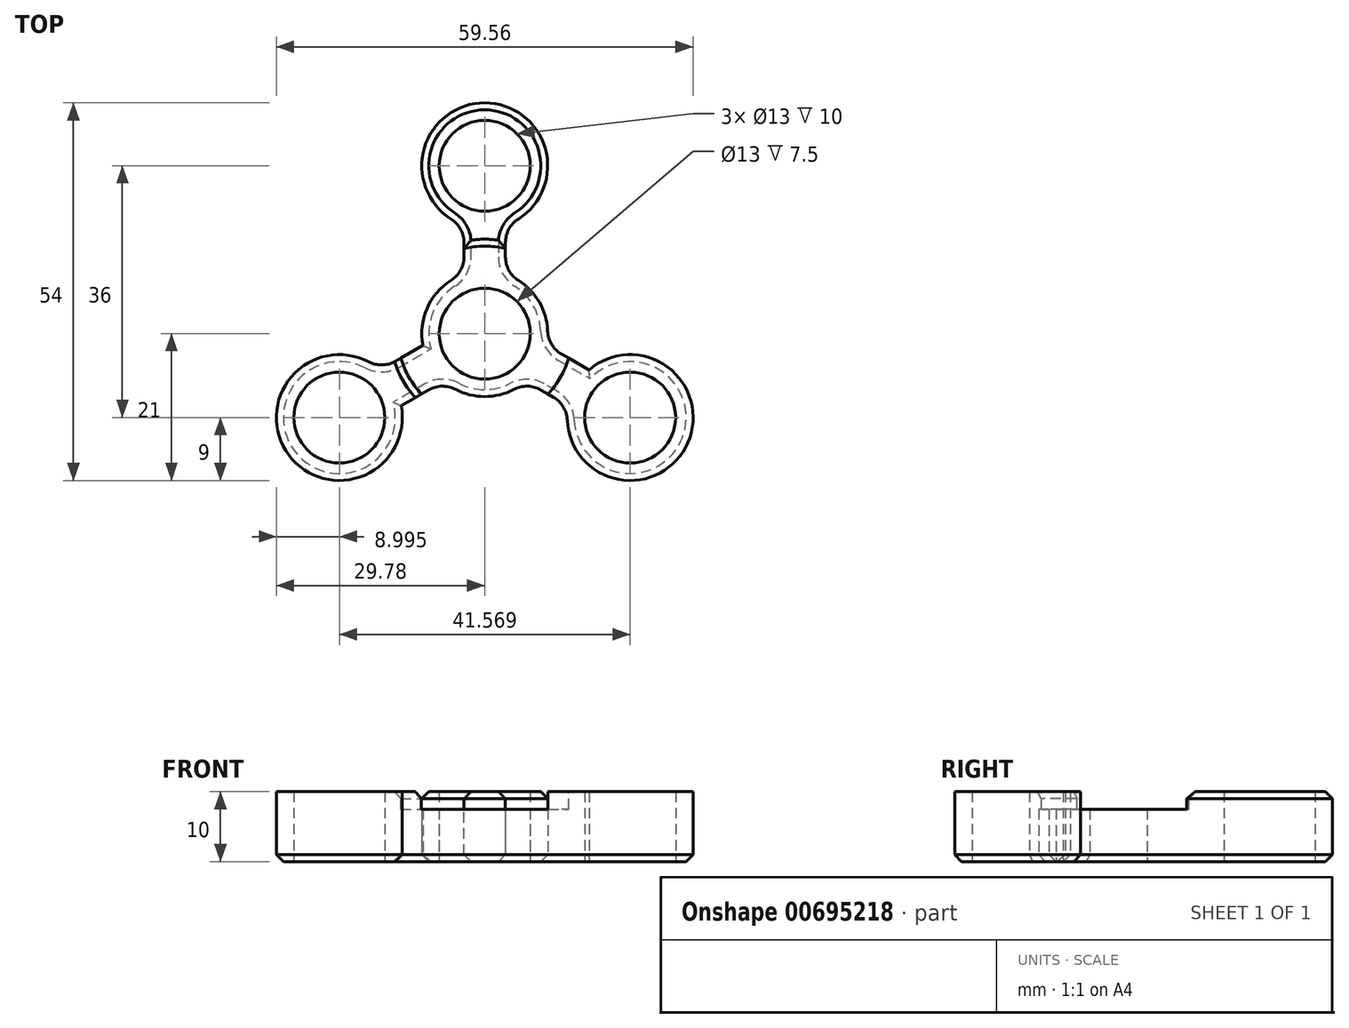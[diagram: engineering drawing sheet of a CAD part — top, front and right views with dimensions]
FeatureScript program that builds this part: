
annotation { "Feature Type Name" : "Feature", "Feature Type Description" : "" }
export const myFeature = defineFeature(function(context is Context, id is Id, definition is map)
    precondition{}
    {
        {
            var Q0;
            Q0=qCreatedBy(makeId("Top.planeOp"),FACE);
            var sketch = newSketch(context, id + "F0", { "sketchPlane" : qUnion([Q0])});
            skLineSegment(sketch, "E0", {"start": v(0, 0) * mm, "end": v(0, 24) * mm, "construction": true});
            skCircle(sketch, "E1", {"center": v(0, 24) * mm, "radius": 6.5 * mm});
            skPoint(sketch, "E2.center", {"position": v(0, 0) * mm});
            skCircle(sketch, "E3", {"center": v(0, 0) * mm, "radius": 6.5 * mm});
            skArc(sketch, "E4", {"start": v(2.96, 15.5) * mm, "mid": v(0, 33) * mm, "end": v(-2.96, 15.5) * mm});
            skCircle(sketch, "E5", {"center": v(0, 0) * mm, "radius": 9 * mm});
            skLineSegment(sketch, "E6", {"start": v(-2.96, 15.5) * mm, "end": v(-2.96, 8.5) * mm});
            skLineSegment(sketch, "E7.MirrorCS", {"start": v(2.96, 15.5) * mm, "end": v(2.96, 8.5) * mm});
            skArc(sketch, "E8.1.0", {"start": v(-14.9, -5.19) * mm, "mid": v(-28.58, -16.5) * mm, "end": v(-11.94, -10.31) * mm});
            skCircle(sketch, "E8.1.1", {"center": v(-20.78, -12) * mm, "radius": 6.5 * mm});
            skLineSegment(sketch, "E8.1.2", {"start": v(-11.94, -10.31) * mm, "end": v(-5.88, -6.81) * mm});
            skLineSegment(sketch, "E8.1.3", {"start": v(-14.9, -5.19) * mm, "end": v(-8.84, -1.69) * mm});
            skArc(sketch, "E8.2.0", {"start": v(11.94, -10.31) * mm, "mid": v(28.58, -16.5) * mm, "end": v(14.9, -5.19) * mm});
            skCircle(sketch, "E8.2.1", {"center": v(20.78, -12) * mm, "radius": 6.5 * mm});
            skLineSegment(sketch, "E8.2.2", {"start": v(14.9, -5.19) * mm, "end": v(8.84, -1.69) * mm});
            skLineSegment(sketch, "E8.2.3", {"start": v(11.94, -10.31) * mm, "end": v(5.88, -6.81) * mm});
            skSolve(sketch);
        }
        {
            var Q0;
            Q0=qSketchRegion(id+"F0",true);
            extrude(context, id + "F1", {"entities" : qUnion([Q0]), "endBound" : BoundingType.SYMMETRIC, "depth" : 10 * mm, "offsetDistance" : 25 * mm});
        }
        {
            var Q0;
            Q0=makeQuery(id+"F1.opExtrude","CAP_FACE",FACE,{"disambiguationData":[OSD([sQuery(id+"F0.wireOp",EDGE,"E1"),sQuery(id+"F0.wireOp",EDGE,"E3"),sQuery(id+"F0.wireOp",EDGE,"E4"),sQuery(id+"F0.wireOp",EDGE,"SNb2FpTf-bqCU-mBP4-37Ot-8CH4sN8bmC5e"),sQuery(id+"F0.wireOp",EDGE,"d9168214-b0ef-4c21-9807-18c6f3a28a83.1.0"),sQuery(id+"F0.wireOp",EDGE,"d9168214-b0ef-4c21-9807-18c6f3a28a83.1.1"),sQuery(id+"F0.wireOp",EDGE,"d9168214-b0ef-4c21-9807-18c6f3a28a83.2.0"),sQuery(id+"F0.wireOp",EDGE,"d9168214-b0ef-4c21-9807-18c6f3a28a83.2.1"),sQuery(id+"F0.wireOp",EDGE,"3bd34c21-cdaa-4902-b1d2-4efe5426a100.trimOffspring"),sQuery(id+"F0.wireOp",EDGE,"9c9765f9-2684-4891-bd0d-f60ce666e364.trimOffspring")])],"isStart":false});
            var sketch = newSketch(context, id + "F2", { "sketchPlane" : qUnion([Q0])});
            skCircle(sketch, "E9", {"center": v(0, 0) * mm, "radius": 12.5 * mm});
            skSolve(sketch);
        }
        {
            var Q0;
            Q0=qSketchRegion(id+"F2",true);
            extrude(context, id + "F3", {"entities" : qUnion([Q0]), "operationType" : NewBodyOperationType.REMOVE, "oppositeDirection" : true, "depth" : 2.5 * mm, "offsetDistance" : 25 * mm});
        }
        {
            var Q0;
            Q0=makeQuery(id+"F1.opExtrude","SWEPT_EDGE",EDGE,{"disambiguationData":[OSD([sQuery(id+"F0.wireOp",EDGE,"E4"),sQuery(id+"F0.wireOp",EDGE,"SNb2FpTf-bqCU-mBP4-37Ot-8CH4sN8bmC5e")])]});
            var Q1;
            Q1=makeQuery(id+"F1.opExtrude","SWEPT_EDGE",EDGE,{"disambiguationData":[OSD([sQuery(id+"F0.wireOp",EDGE,"E4"),sQuery(id+"F0.wireOp",EDGE,"9c9765f9-2684-4891-bd0d-f60ce666e364.trimOffspring")])]});
            var Q2;
            Q2=makeQuery(id+"F1.opExtrude","SWEPT_EDGE",EDGE,{"disambiguationData":[OSD([sQuery(id+"F0.wireOp",EDGE,"SNb2FpTf-bqCU-mBP4-37Ot-8CH4sN8bmC5e"),sQuery(id+"F0.wireOp",EDGE,"d9168214-b0ef-4c21-9807-18c6f3a28a83.1.0")])]});
            var Q3;
            Q3=makeQuery(id+"F1.opExtrude","SWEPT_EDGE",EDGE,{"disambiguationData":[OSD([sQuery(id+"F0.wireOp",EDGE,"d9168214-b0ef-4c21-9807-18c6f3a28a83.2.0"),sQuery(id+"F0.wireOp",EDGE,"9c9765f9-2684-4891-bd0d-f60ce666e364.trimOffspring")])]});
            var Q4;
            Q4=makeQuery(id+"F1.opExtrude","SWEPT_EDGE",EDGE,{"disambiguationData":[OSD([sQuery(id+"F0.wireOp",EDGE,"d9168214-b0ef-4c21-9807-18c6f3a28a83.2.0"),sQuery(id+"F0.wireOp",EDGE,"3bd34c21-cdaa-4902-b1d2-4efe5426a100.trimOffspring")])]});
            var Q5;
            Q5=makeQuery(id+"F1.opExtrude","SWEPT_EDGE",EDGE,{"disambiguationData":[OSD([sQuery(id+"F0.wireOp",EDGE,"d9168214-b0ef-4c21-9807-18c6f3a28a83.1.0"),sQuery(id+"F0.wireOp",EDGE,"3bd34c21-cdaa-4902-b1d2-4efe5426a100.trimOffspring")])]});
            var Q6;
            Q6=makeQuery(id+"F1.opExtrude","SWEPT_EDGE",EDGE,{"disambiguationData":[OSD([sQuery(id+"F0.wireOp",EDGE,"E5"),sQuery(id+"F0.wireOp",EDGE,"E6")])]});
            var Q7;
            Q7=makeQuery(id+"F1.opExtrude","SWEPT_EDGE",EDGE,{"disambiguationData":[OSD([sQuery(id+"F0.wireOp",EDGE,"E8.1.0"),sQuery(id+"F0.wireOp",EDGE,"E8.1.3")])]});
            var Q8;
            Q8=makeQuery(id+"F1.opExtrude","SWEPT_EDGE",EDGE,{"disambiguationData":[OSD([sQuery(id+"F0.wireOp",EDGE,"E8.2.0"),sQuery(id+"F0.wireOp",EDGE,"E8.2.3")])]});
            var Q9;
            Q9=makeQuery(id+"F1.opExtrude","SWEPT_EDGE",EDGE,{"disambiguationData":[OSD([sQuery(id+"F0.wireOp",EDGE,"E5"),sQuery(id+"F0.wireOp",EDGE,"E8.1.2")])]});
            var Q10;
            Q10=makeQuery(id+"F1.opExtrude","SWEPT_EDGE",EDGE,{"disambiguationData":[OSD([sQuery(id+"F0.wireOp",EDGE,"E5"),sQuery(id+"F0.wireOp",EDGE,"E8.2.3")])]});
            var Q11;
            Q11=makeQuery(id+"F1.opExtrude","SWEPT_EDGE",EDGE,{"disambiguationData":[OSD([sQuery(id+"F0.wireOp",EDGE,"E5"),sQuery(id+"F0.wireOp",EDGE,"E8.2.2")])]});
            var Q12;
            Q12=makeQuery(id+"F1.opExtrude","SWEPT_EDGE",EDGE,{"disambiguationData":[OSD([sQuery(id+"F0.wireOp",EDGE,"E5"),sQuery(id+"F0.wireOp",EDGE,"E7.MirrorCS")])]});
            fillet(context, id + "F4", {"entities" : qUnion([Q0, Q1, Q2, Q3, Q4, Q5, Q6, Q7, Q8, Q9, Q10, Q11, Q12]), "radius" : 4 * mm, "tangentPropagation" : true, "allowEdgeOverflow" : false});
        }
        {
            var Q0;
            Q0=makeQuery(id+"F1.opExtrude","CAP_EDGE",EDGE,{"disambiguationData":[OSD([sQuery(id+"F0.wireOp",EDGE,"E4")])],"isStart":false});
            var Q1;
            {var subQ1=sQuery(id+"F0.wireOp",EDGE,"E6");var subQ2=sQuery(id+"F2.wireOp",EDGE,"E9");Q1=makeQuery(id+"F3.boolean.opBoolean","COPY",EDGE,{"disambiguationData":[TD([makeQuery(id+"F1.opExtrude","SWEPT_FACE",FACE,{"disambiguationData":[OSD([subQ1])]})])],"derivedFrom":makeQuery(id+"F3.opExtrude","CAP_EDGE",EDGE,{"disambiguationData":[OSD([subQ2])],"isStart":true})});}
            var Q2;
            {var subQ1=sQuery(id+"F0.wireOp",EDGE,"E8.1.2");var subQ2=sQuery(id+"F2.wireOp",EDGE,"E9");Q2=makeQuery(id+"F3.boolean.opBoolean","COPY",EDGE,{"disambiguationData":[TD([makeQuery(id+"F1.opExtrude","SWEPT_FACE",FACE,{"disambiguationData":[OSD([subQ1])]})])],"derivedFrom":makeQuery(id+"F3.opExtrude","CAP_EDGE",EDGE,{"disambiguationData":[OSD([subQ2])],"isStart":true})});}
            var Q3;
            {var subQ1=sQuery(id+"F0.wireOp",EDGE,"E8.2.2");var subQ2=sQuery(id+"F2.wireOp",EDGE,"E9");Q3=makeQuery(id+"F3.boolean.opBoolean","COPY",EDGE,{"disambiguationData":[TD([makeQuery(id+"F1.opExtrude","SWEPT_FACE",FACE,{"disambiguationData":[OSD([subQ1])]})])],"derivedFrom":makeQuery(id+"F3.opExtrude","CAP_EDGE",EDGE,{"disambiguationData":[OSD([subQ2])],"isStart":true})});}
            var Q4;
            {var subQ1=sQuery(id+"F0.wireOp",EDGE,"E8.2.2");var subQ2=sQuery(id+"F2.wireOp",EDGE,"E9");Q4=makeQuery(id+"F4SlQ3XEbq7tBdr_1.1.F3.boolean.opBoolean","COPY",EDGE,{"disambiguationData":[TD([makeQuery(id+"F1.opExtrude","SWEPT_FACE",FACE,{"disambiguationData":[OSD([subQ1])]})])],"derivedFrom":makeQuery(id+"F4SlQ3XEbq7tBdr_1.1.F3.opExtrude","CAP_EDGE",EDGE,{"disambiguationData":[OSD([subQ2])],"isStart":true})});}
            var Q5;
            {var subQ1=sQuery(id+"F0.wireOp",EDGE,"E8.1.2");var subQ2=sQuery(id+"F2.wireOp",EDGE,"E9");Q5=makeQuery(id+"F4SlQ3XEbq7tBdr_1.1.F3.boolean.opBoolean","COPY",EDGE,{"disambiguationData":[TD([makeQuery(id+"F1.opExtrude","SWEPT_FACE",FACE,{"disambiguationData":[OSD([subQ1])]})])],"derivedFrom":makeQuery(id+"F4SlQ3XEbq7tBdr_1.1.F3.opExtrude","CAP_EDGE",EDGE,{"disambiguationData":[OSD([subQ2])],"isStart":true})});}
            var Q6;
            {var subQ1=sQuery(id+"F0.wireOp",EDGE,"E6");var subQ2=sQuery(id+"F2.wireOp",EDGE,"E9");Q6=makeQuery(id+"F4SlQ3XEbq7tBdr_1.1.F3.boolean.opBoolean","COPY",EDGE,{"disambiguationData":[TD([makeQuery(id+"F1.opExtrude","SWEPT_FACE",FACE,{"disambiguationData":[OSD([subQ1])]})])],"derivedFrom":makeQuery(id+"F4SlQ3XEbq7tBdr_1.1.F3.opExtrude","CAP_EDGE",EDGE,{"disambiguationData":[OSD([subQ2])],"isStart":true})});}
            var Q7;
            Q7=makeQuery(id+"F1.opExtrude","CAP_EDGE",EDGE,{"disambiguationData":[OSD([sQuery(id+"F0.wireOp",EDGE,"E8.1.0")])],"isStart":true});
            var Q8;
            Q8=makeQuery(id+"F1.opExtrude","CAP_EDGE",EDGE,{"disambiguationData":[OSD([sQuery(id+"F0.wireOp",EDGE,"E8.2.0")])],"isStart":true});
            var Q9;
            Q9=makeQuery(id+"F1.opExtrude","CAP_EDGE",EDGE,{"disambiguationData":[OSD([sQuery(id+"F0.wireOp",EDGE,"E4")])],"isStart":true});
            chamfer(context, id + "F5", {"entities" : qUnion([Q0, Q1, Q2, Q3, Q4, Q5, Q6, Q7, Q8, Q9]), "width" : 1 * mm, "tangentPropagation" : true});
        }
    });
